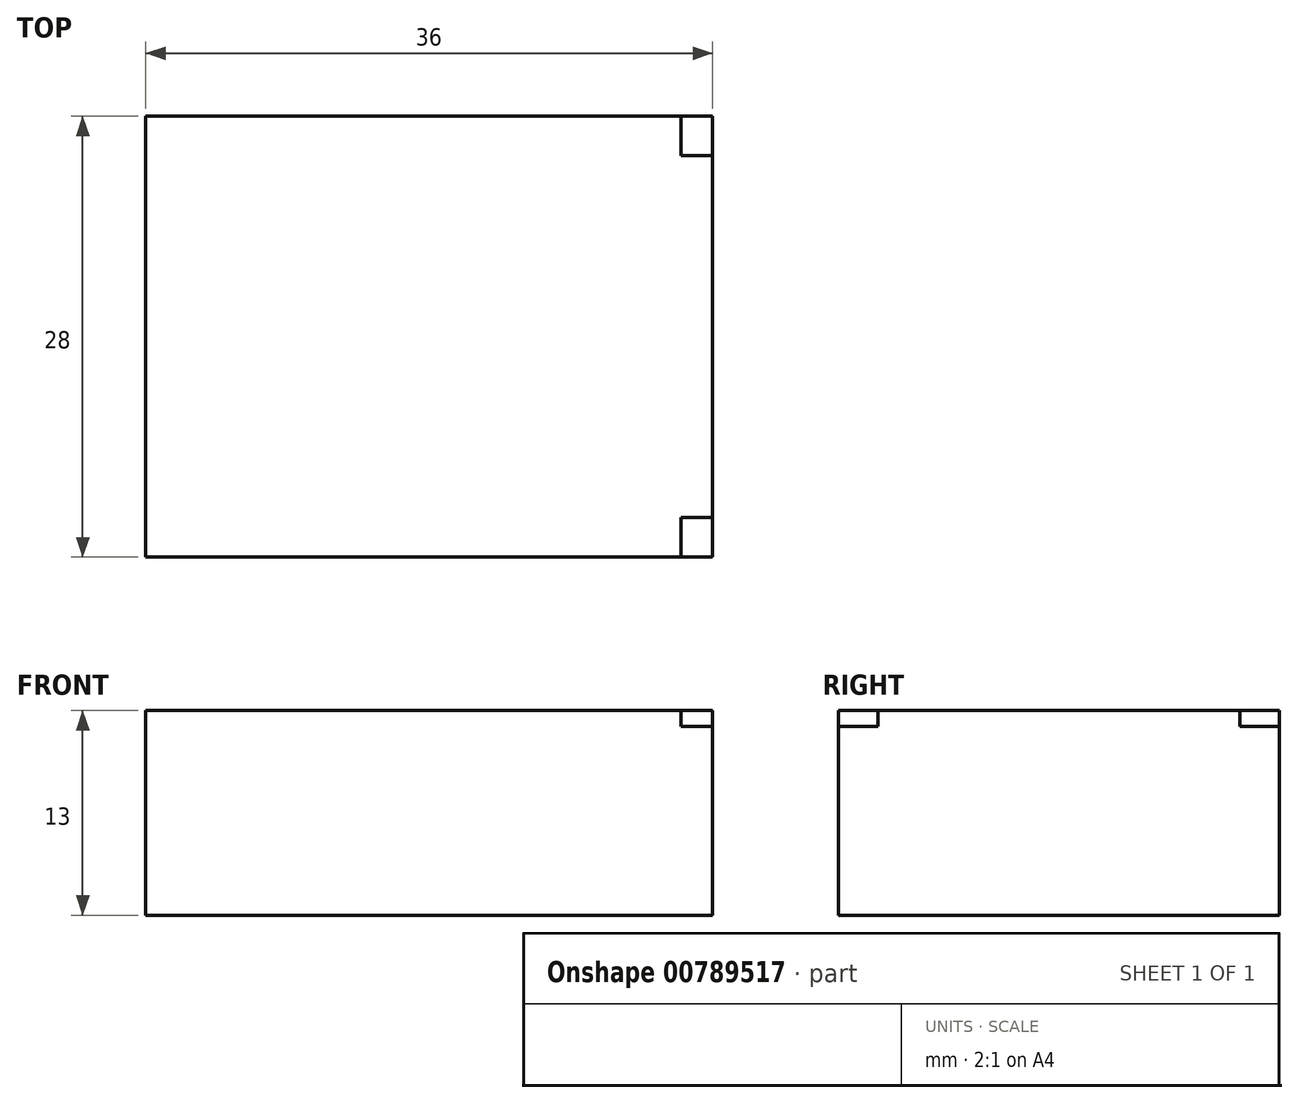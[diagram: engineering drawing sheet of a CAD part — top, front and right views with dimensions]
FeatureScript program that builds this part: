
annotation { "Feature Type Name" : "Feature", "Feature Type Description" : "" }
export const myFeature = defineFeature(function(context is Context, id is Id, definition is map)
    precondition{}
    {
        {
            var Q0;
            Q0=qCreatedBy(makeId("Top.planeOp"),FACE);
            var sketch = newSketch(context, id + "F0", { "sketchPlane" : qUnion([Q0])});
            skLineSegment(sketch, "E0.bottom", {"start": v(18, -14) * mm, "end": v(-18, -14) * mm});
            skLineSegment(sketch, "E0.top", {"start": v(18, 14) * mm, "end": v(-18, 14) * mm});
            skLineSegment(sketch, "E0.left", {"start": v(18, -14) * mm, "end": v(18, 14) * mm});
            skLineSegment(sketch, "E0.right", {"start": v(-18, -14) * mm, "end": v(-18, 14) * mm});
            skPoint(sketch, "E0.middle", {"position": v(0, 0) * mm});
            skSolve(sketch);
        }
        {
            var Q0;
            Q0 = qSketchRegion(id + "F0", true);
            extrude(context, id + "F1", {"entities" : qUnion([Q0]), "depth" : 13 * mm, "offsetDistance" : 25 * mm});
        }
        {
            var Q0;
            Q0=makeQuery(id+"F1.opExtrude","CAP_FACE",FACE,{"disambiguationData":[OSD([sQuery(id+"F0.wireOp",EDGE,"E0.bottom"),sQuery(id+"F0.wireOp",EDGE,"E0.top"),sQuery(id+"F0.wireOp",EDGE,"E0.left"),sQuery(id+"F0.wireOp",EDGE,"E0.right")])],"isStart":false});
            var sketch = newSketch(context, id + "F2", { "sketchPlane" : qUnion([Q0])});
            skLineSegment(sketch, "E1.bottom", {"start": v(18, 14) * mm, "end": v(16, 14) * mm});
            skLineSegment(sketch, "E1.top", {"start": v(18, 11.5) * mm, "end": v(16, 11.5) * mm});
            skLineSegment(sketch, "E1.left", {"start": v(18, 14) * mm, "end": v(18, 11.5) * mm});
            skLineSegment(sketch, "E1.right", {"start": v(16, 14) * mm, "end": v(16, 11.5) * mm});
            skLineSegment(sketch, "E2", {"start": v(-18, 0) * mm, "end": v(18, 0) * mm, "construction": true});
            skLineSegment(sketch, "E3.MirrorCS", {"start": v(16, -14) * mm, "end": v(16, -11.5) * mm});
            skLineSegment(sketch, "E4.MirrorCS", {"start": v(18, -14) * mm, "end": v(18, -11.5) * mm});
            skLineSegment(sketch, "E5.MirrorCS", {"start": v(18, -14) * mm, "end": v(16, -14) * mm});
            skLineSegment(sketch, "E6.MirrorCS", {"start": v(18, -11.5) * mm, "end": v(16, -11.5) * mm});
            skSolve(sketch);
        }
        {
            var Q0;
            Q0=makeQuery(id+"F2.imprint","IMPRINT",FACE,{"disambiguationData":[TD([[makeQuery(id+"F2.imprint","IMPRINT",EDGE,{"derivedFrom":sQuery(id+"F2.wireOp",EDGE,"E3.MirrorCS")}),-1.0]])]});
            var Q1;
            Q1=makeQuery(id+"F2.imprint","IMPRINT",FACE,{"disambiguationData":[TD([[makeQuery(id+"F2.imprint","IMPRINT",EDGE,{"derivedFrom":sQuery(id+"F2.wireOp",EDGE,"E1.bottom")}),1.0]])]});
            extrude(context, id + "F3", {"entities" : qUnion([Q0, Q1]), "operationType" : NewBodyOperationType.REMOVE, "oppositeDirection" : true, "depth" : 1 * mm, "offsetDistance" : 25 * mm});
        }
    });
